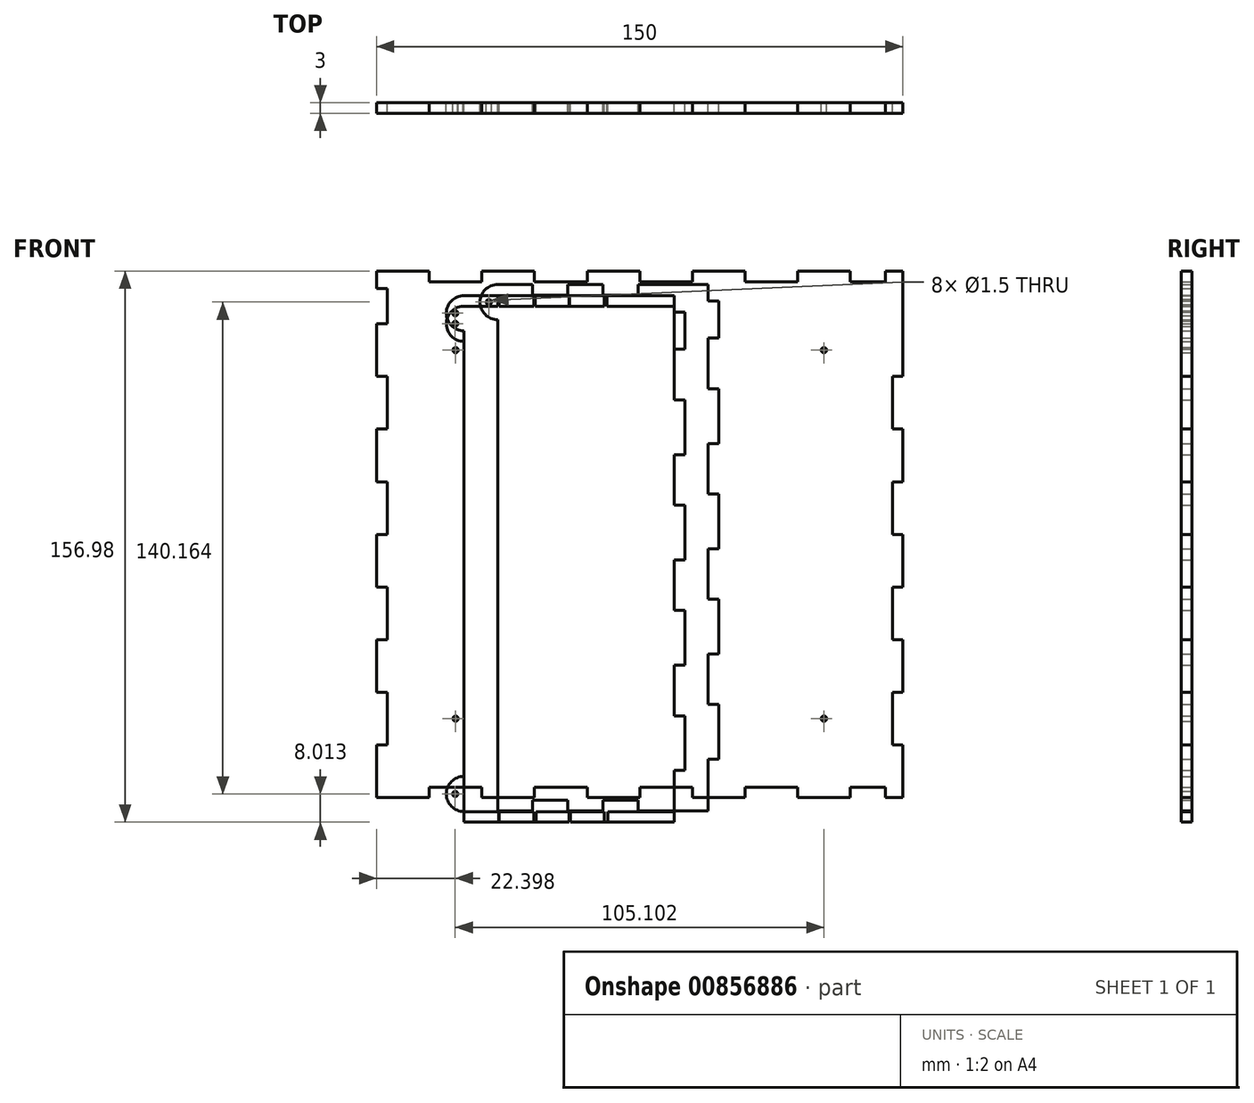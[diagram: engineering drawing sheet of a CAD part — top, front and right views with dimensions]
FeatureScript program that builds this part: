
annotation { "Feature Type Name" : "Feature", "Feature Type Description" : "" }
export const myFeature = defineFeature(function(context is Context, id is Id, definition is map)
    precondition{}
    {
        {
            var Q0;
            Q0=qCreatedBy(makeId("Front.planeOp"),FACE);
            var sketch = newSketch(context, id + "F0", { "sketchPlane" : qUnion([Q0])});
            skPoint(sketch, "E0.middle", {"position": v(0, 0) * mm});
            skLineSegment(sketch, "E1", {"start": v(-60, 72) * mm, "end": v(-45, 72) * mm});
            skLineSegment(sketch, "E2", {"start": v(-75, 75) * mm, "end": v(-60, 75) * mm});
            skLineSegment(sketch, "E3", {"start": v(-60, 75) * mm, "end": v(-60, 72) * mm});
            skLineSegment(sketch, "E4", {"start": v(-45, 72) * mm, "end": v(-45, 75) * mm});
            skLineSegment(sketch, "E5", {"start": v(-45, 75) * mm, "end": v(-30, 75) * mm});
            skLineSegment(sketch, "E6", {"start": v(-30, 75) * mm, "end": v(-30, 72) * mm});
            skLineSegment(sketch, "E7", {"start": v(-30, 72) * mm, "end": v(-15, 72) * mm});
            skLineSegment(sketch, "E8", {"start": v(-15, 72) * mm, "end": v(-15, 75) * mm});
            skLineSegment(sketch, "E9", {"start": v(-15, 75) * mm, "end": v(0, 75) * mm});
            skLineSegment(sketch, "E10", {"start": v(0, 75) * mm, "end": v(0, 72) * mm});
            skLineSegment(sketch, "E11", {"start": v(0, 72) * mm, "end": v(15, 72) * mm});
            skLineSegment(sketch, "E12", {"start": v(15, 72) * mm, "end": v(15, 75) * mm});
            skLineSegment(sketch, "E13", {"start": v(15, 75) * mm, "end": v(30, 75) * mm});
            skLineSegment(sketch, "E14", {"start": v(30, 75) * mm, "end": v(30, 72) * mm});
            skLineSegment(sketch, "E15", {"start": v(30, 72) * mm, "end": v(45, 72) * mm});
            skLineSegment(sketch, "E16", {"start": v(45, 72) * mm, "end": v(45, 75) * mm});
            skLineSegment(sketch, "E17", {"start": v(45, 75) * mm, "end": v(60, 75) * mm});
            skLineSegment(sketch, "E18", {"start": v(60, 75) * mm, "end": v(60, 72) * mm});
            skLineSegment(sketch, "E19", {"start": v(60, 72) * mm, "end": v(70, 72) * mm});
            skLineSegment(sketch, "E20", {"start": v(70, 72) * mm, "end": v(70, 75) * mm});
            skLineSegment(sketch, "E21", {"start": v(70, 75) * mm, "end": v(75, 75) * mm});
            skLineSegment(sketch, "E22", {"start": v(-72, -60) * mm, "end": v(-72, -45) * mm});
            skLineSegment(sketch, "E23", {"start": v(-75, -75) * mm, "end": v(-75, -60) * mm});
            skLineSegment(sketch, "E24", {"start": v(-75, -60) * mm, "end": v(-72, -60) * mm});
            skLineSegment(sketch, "E25", {"start": v(-72, -45) * mm, "end": v(-75, -45) * mm});
            skLineSegment(sketch, "E26", {"start": v(-75, -45) * mm, "end": v(-75, -30) * mm});
            skLineSegment(sketch, "E27", {"start": v(-75, -30) * mm, "end": v(-72, -30) * mm});
            skLineSegment(sketch, "E28", {"start": v(-72, -30) * mm, "end": v(-72, -15) * mm});
            skLineSegment(sketch, "E29", {"start": v(-72, -15) * mm, "end": v(-75, -15) * mm});
            skLineSegment(sketch, "E30", {"start": v(-75, -15) * mm, "end": v(-75, 0) * mm});
            skLineSegment(sketch, "E31", {"start": v(-75, 0) * mm, "end": v(-72, 0) * mm});
            skLineSegment(sketch, "E32", {"start": v(-72, 0) * mm, "end": v(-72, 15) * mm});
            skLineSegment(sketch, "E33", {"start": v(-72, 15) * mm, "end": v(-75, 15) * mm});
            skLineSegment(sketch, "E34", {"start": v(-75, 15) * mm, "end": v(-75, 30) * mm});
            skLineSegment(sketch, "E35", {"start": v(-75, 30) * mm, "end": v(-72, 30) * mm});
            skLineSegment(sketch, "E36", {"start": v(-72, 30) * mm, "end": v(-72, 45) * mm});
            skLineSegment(sketch, "E37", {"start": v(-72, 45) * mm, "end": v(-75, 45) * mm});
            skLineSegment(sketch, "E38", {"start": v(-75, 45) * mm, "end": v(-75, 60) * mm});
            skPoint(sketch, "E39.trimOffspring.end.orphan", {"position": v(-72, 75) * mm});
            skLineSegment(sketch, "E40", {"start": v(-75, 60) * mm, "end": v(-72, 60) * mm});
            skLineSegment(sketch, "E41", {"start": v(-72, 60) * mm, "end": v(-72, 70) * mm});
            skLineSegment(sketch, "E42", {"start": v(-72, 70) * mm, "end": v(-75, 70) * mm});
            skLineSegment(sketch, "E43", {"start": v(-75, 70) * mm, "end": v(-75, 75) * mm});
            skLineSegment(sketch, "E44", {"start": v(-75, 75) * mm, "end": v(-72, 75) * mm});
            skLineSegment(sketch, "E45.MirrorCS", {"start": v(75, 30) * mm, "end": v(72, 30) * mm});
            skLineSegment(sketch, "E46.MirrorCS", {"start": v(72, 45) * mm, "end": v(75, 45) * mm});
            skLineSegment(sketch, "E47.MirrorCS", {"start": v(75, 0) * mm, "end": v(72, 0) * mm});
            skLineSegment(sketch, "E48.MirrorCS", {"start": v(75, -60) * mm, "end": v(72, -60) * mm});
            skLineSegment(sketch, "E49.MirrorCS", {"start": v(72, 15) * mm, "end": v(75, 15) * mm});
            skLineSegment(sketch, "E50.MirrorCS", {"start": v(72, -45) * mm, "end": v(75, -45) * mm});
            skLineSegment(sketch, "E51.MirrorCS", {"start": v(75, -75) * mm, "end": v(75, -72) * mm});
            skLineSegment(sketch, "E52.MirrorCS", {"start": v(75, -30) * mm, "end": v(72, -30) * mm});
            skLineSegment(sketch, "E53.MirrorCS", {"start": v(75, 70) * mm, "end": v(75, 75) * mm});
            skLineSegment(sketch, "E54.MirrorCS", {"start": v(75, -75) * mm, "end": v(75, -60) * mm});
            skLineSegment(sketch, "E55.MirrorCS", {"start": v(72, -15) * mm, "end": v(75, -15) * mm});
            skLineSegment(sketch, "E56.MirrorCS", {"start": v(72, 0) * mm, "end": v(72, 15) * mm});
            skLineSegment(sketch, "E57.MirrorCS", {"start": v(72, 30) * mm, "end": v(72, 45) * mm});
            skLineSegment(sketch, "E58.MirrorCS", {"start": v(72, -60) * mm, "end": v(72, -45) * mm});
            skLineSegment(sketch, "E59.MirrorCS", {"start": v(72, -30) * mm, "end": v(72, -15) * mm});
            skLineSegment(sketch, "E60.MirrorCS", {"start": v(75, 15) * mm, "end": v(75, 30) * mm});
            skLineSegment(sketch, "E61.MirrorCS", {"start": v(75, -15) * mm, "end": v(75, 0) * mm});
            skPoint(sketch, "E62.MirrorP", {"position": v(75, -72) * mm});
            skLineSegment(sketch, "E63.MirrorCS", {"start": v(75, 45) * mm, "end": v(75, 60) * mm});
            skLineSegment(sketch, "E64.MirrorCS", {"start": v(75, -45) * mm, "end": v(75, -30) * mm});
            skLineSegment(sketch, "E65", {"start": v(75, 70) * mm, "end": v(75, 60) * mm});
            skPoint(sketch, "E66.start.orphan", {"position": v(-102.84, -173.45) * mm});
            skLineSegment(sketch, "E67.MirrorCS", {"start": v(45, -72) * mm, "end": v(45, -75) * mm});
            skLineSegment(sketch, "E68.MirrorCS", {"start": v(60, -75) * mm, "end": v(60, -72) * mm});
            skLineSegment(sketch, "E69.MirrorCS", {"start": v(15, -72) * mm, "end": v(15, -75) * mm});
            skLineSegment(sketch, "E70.MirrorCS", {"start": v(-60, -75) * mm, "end": v(-60, -72) * mm});
            skLineSegment(sketch, "E71.MirrorCS", {"start": v(-30, -75) * mm, "end": v(-30, -72) * mm});
            skLineSegment(sketch, "E72.MirrorCS", {"start": v(-15, -72) * mm, "end": v(-15, -75) * mm});
            skLineSegment(sketch, "E73.MirrorCS", {"start": v(0, -75) * mm, "end": v(0, -72) * mm});
            skLineSegment(sketch, "E74.MirrorCS", {"start": v(30, -75) * mm, "end": v(30, -72) * mm});
            skLineSegment(sketch, "E75.MirrorCS", {"start": v(-45, -72) * mm, "end": v(-45, -75) * mm});
            skLineSegment(sketch, "E76.MirrorCS", {"start": v(70, -72) * mm, "end": v(70, -75) * mm});
            skLineSegment(sketch, "E77.MirrorCS", {"start": v(-75, -75) * mm, "end": v(-72, -75) * mm});
            skLineSegment(sketch, "E78.MirrorCS", {"start": v(0, -72) * mm, "end": v(15, -72) * mm});
            skLineSegment(sketch, "E79.MirrorCS", {"start": v(70, -75) * mm, "end": v(75, -75) * mm});
            skLineSegment(sketch, "E80.MirrorCS", {"start": v(30, -72) * mm, "end": v(45, -72) * mm});
            skLineSegment(sketch, "E81.MirrorCS", {"start": v(-60, -72) * mm, "end": v(-45, -72) * mm});
            skLineSegment(sketch, "E82.MirrorCS", {"start": v(15, -75) * mm, "end": v(30, -75) * mm});
            skLineSegment(sketch, "E83.MirrorCS", {"start": v(-15, -75) * mm, "end": v(0, -75) * mm});
            skLineSegment(sketch, "E84.MirrorCS", {"start": v(45, -75) * mm, "end": v(60, -75) * mm});
            skLineSegment(sketch, "E85.MirrorCS", {"start": v(-75, -75) * mm, "end": v(-60, -75) * mm});
            skLineSegment(sketch, "E86.MirrorCS", {"start": v(-45, -75) * mm, "end": v(-30, -75) * mm});
            skLineSegment(sketch, "E87.MirrorCS", {"start": v(-30, -72) * mm, "end": v(-15, -72) * mm});
            skLineSegment(sketch, "E88.MirrorCS", {"start": v(60, -72) * mm, "end": v(70, -72) * mm});
            skPoint(sketch, "E89.MirrorP", {"position": v(-72, -75) * mm});
            skCircle(sketch, "E90", {"center": v(-52.5, -52.5) * mm, "radius": 0.75 * mm});
            skCircle(sketch, "E91", {"center": v(-52.5, 52.5) * mm, "radius": 0.75 * mm});
            skCircle(sketch, "E92", {"center": v(52.5, 52.5) * mm, "radius": 0.75 * mm});
            skCircle(sketch, "E93", {"center": v(52.5, -52.5) * mm, "radius": 0.75 * mm});
            skSolve(sketch);
        }
        {
            var Q0;
            Q0=qCreatedBy(makeId("Front.planeOp"),FACE);
            var sketch = newSketch(context, id + "F1", { "sketchPlane" : qUnion([Q0])});
            skPoint(sketch, "E94.start.orphan", {"position": v(-103.07, -194.53) * mm});
            skLineSegment(sketch, "E95", {"start": v(22.48, -63.79) * mm, "end": v(22.48, -48.79) * mm});
            skLineSegment(sketch, "E96", {"start": v(19.48, -78.79) * mm, "end": v(19.48, -64.09) * mm});
            skLineSegment(sketch, "E97", {"start": v(19.48, -48.49) * mm, "end": v(19.48, -34.09) * mm});
            skLineSegment(sketch, "E98", {"start": v(22.48, -33.79) * mm, "end": v(22.48, -18.79) * mm});
            skLineSegment(sketch, "E99", {"start": v(19.48, -18.49) * mm, "end": v(19.48, -4.09) * mm});
            skLineSegment(sketch, "E100", {"start": v(22.48, -3.79) * mm, "end": v(22.48, 11.21) * mm});
            skLineSegment(sketch, "E101", {"start": v(19.48, 11.51) * mm, "end": v(19.48, 25.91) * mm});
            skLineSegment(sketch, "E102", {"start": v(22.48, 26.21) * mm, "end": v(22.48, 41.21) * mm});
            skLineSegment(sketch, "E103", {"start": v(19.48, 41.51) * mm, "end": v(19.48, 55.91) * mm});
            skLineSegment(sketch, "E104", {"start": v(19.48, 66.51) * mm, "end": v(19.48, 71.21) * mm});
            skLineSegment(sketch, "E105", {"start": v(19.48, 71.21) * mm, "end": v(-0.52, 71.21) * mm});
            skLineSegment(sketch, "E106", {"start": v(-40.52, 61.19) * mm, "end": v(-40.52, -78.79) * mm});
            skLineSegment(sketch, "E107", {"start": v(19.48, -48.49) * mm, "end": v(22.48, -48.49) * mm});
            skLineSegment(sketch, "E108", {"start": v(22.48, -48.49) * mm, "end": v(22.48, -48.79) * mm});
            skPoint(sketch, "E109.start.orphan", {"position": v(19.48, -48.79) * mm});
            skLineSegment(sketch, "E110", {"start": v(19.48, -64.09) * mm, "end": v(22.48, -64.09) * mm});
            skLineSegment(sketch, "E111", {"start": v(22.48, -64.09) * mm, "end": v(22.48, -63.79) * mm});
            skLineSegment(sketch, "E112", {"start": v(19.48, -34.09) * mm, "end": v(22.48, -34.09) * mm});
            skLineSegment(sketch, "E113", {"start": v(22.48, -34.09) * mm, "end": v(22.48, -33.79) * mm});
            skLineSegment(sketch, "E114", {"start": v(19.48, -18.49) * mm, "end": v(22.48, -18.49) * mm});
            skLineSegment(sketch, "E115", {"start": v(22.48, -18.49) * mm, "end": v(22.48, -18.79) * mm});
            skPoint(sketch, "E116.orphan", {"position": v(19.48, -18.79) * mm});
            skLineSegment(sketch, "E117", {"start": v(22.48, -3.79) * mm, "end": v(22.48, -4.09) * mm});
            skLineSegment(sketch, "E118", {"start": v(22.48, -4.09) * mm, "end": v(19.48, -4.09) * mm});
            skLineSegment(sketch, "E119", {"start": v(22.48, 11.21) * mm, "end": v(22.48, 11.51) * mm});
            skLineSegment(sketch, "E120", {"start": v(22.48, 11.51) * mm, "end": v(19.48, 11.51) * mm});
            skLineSegment(sketch, "E121", {"start": v(22.48, 41.21) * mm, "end": v(22.48, 41.51) * mm});
            skLineSegment(sketch, "E122", {"start": v(22.48, 41.51) * mm, "end": v(19.48, 41.51) * mm});
            skLineSegment(sketch, "E123", {"start": v(22.48, 26.21) * mm, "end": v(22.48, 25.91) * mm});
            skLineSegment(sketch, "E124", {"start": v(22.48, 25.91) * mm, "end": v(19.48, 25.91) * mm});
            skPoint(sketch, "E125", {"position": v(-60.53, 71.19) * mm});
            skArc(sketch, "E126", {"start": v(-40.52, 71.21) * mm, "mid": v(-45.53, 66.2) * mm, "end": v(-40.52, 61.19) * mm});
            skCircle(sketch, "E127", {"center": v(-43, 66.2) * mm, "radius": 0.75 * mm});
            skPoint(sketch, "E128.orphan", {"position": v(-60.53, 66.19) * mm});
            skPoint(sketch, "E129.start.orphan", {"position": v(-60.53, 61.19) * mm});
            skLineSegment(sketch, "E130", {"start": v(-40.52, 71.21) * mm, "end": v(-30.52, 71.21) * mm});
            skLineSegment(sketch, "E131", {"start": v(-30.52, 71.21) * mm, "end": v(-30.52, 68.21) * mm});
            skLineSegment(sketch, "E132", {"start": v(-30.52, 68.21) * mm, "end": v(-20.52, 68.21) * mm});
            skLineSegment(sketch, "E133", {"start": v(-20.52, 68.21) * mm, "end": v(-20.52, 71.21) * mm});
            skLineSegment(sketch, "E134", {"start": v(-20.52, 71.21) * mm, "end": v(-10.52, 71.21) * mm});
            skLineSegment(sketch, "E135", {"start": v(-10.52, 71.21) * mm, "end": v(-10.52, 68.21) * mm});
            skLineSegment(sketch, "E136", {"start": v(-10.52, 68.21) * mm, "end": v(-0.52, 68.21) * mm});
            skLineSegment(sketch, "E137", {"start": v(-0.52, 68.21) * mm, "end": v(-0.52, 71.21) * mm});
            skLineSegment(sketch, "E138.trimOffspring", {"start": v(-30.52, 71.21) * mm, "end": v(-40.52, 71.21) * mm});
            skLineSegment(sketch, "E139.trimOffspring", {"start": v(-10.52, 71.21) * mm, "end": v(-20.52, 71.21) * mm});
            skLineSegment(sketch, "E140.MirrorCS", {"start": v(-10.52, -78.79) * mm, "end": v(-10.52, -75.79) * mm});
            skLineSegment(sketch, "E141.MirrorCS", {"start": v(-20.52, -75.79) * mm, "end": v(-20.52, -78.79) * mm});
            skLineSegment(sketch, "E142.MirrorCS", {"start": v(-0.52, -75.79) * mm, "end": v(-0.52, -78.79) * mm});
            skLineSegment(sketch, "E143.MirrorCS", {"start": v(-30.52, -78.79) * mm, "end": v(-30.52, -75.79) * mm});
            skLineSegment(sketch, "E144.MirrorCS", {"start": v(-10.52, -78.79) * mm, "end": v(-20.52, -78.79) * mm});
            skLineSegment(sketch, "E145.MirrorCS", {"start": v(-40.52, -78.79) * mm, "end": v(-30.52, -78.79) * mm});
            skLineSegment(sketch, "E146.MirrorCS", {"start": v(-10.52, -75.79) * mm, "end": v(-0.52, -75.79) * mm});
            skLineSegment(sketch, "E147.MirrorCS", {"start": v(-30.52, -78.79) * mm, "end": v(-40.52, -78.79) * mm});
            skLineSegment(sketch, "E148.MirrorCS", {"start": v(-30.52, -75.79) * mm, "end": v(-20.52, -75.79) * mm});
            skLineSegment(sketch, "E149.MirrorCS", {"start": v(19.48, -78.79) * mm, "end": v(-0.52, -78.79) * mm});
            skLineSegment(sketch, "E150.MirrorCS", {"start": v(-20.52, -78.79) * mm, "end": v(-10.52, -78.79) * mm});
            skLineSegment(sketch, "E151", {"start": v(22.48, 56.21) * mm, "end": v(22.48, 66.21) * mm});
            skLineSegment(sketch, "E152", {"start": v(22.48, 66.21) * mm, "end": v(22.48, 66.51) * mm});
            skLineSegment(sketch, "E153", {"start": v(22.48, 66.51) * mm, "end": v(19.48, 66.51) * mm});
            skLineSegment(sketch, "E154", {"start": v(22.48, 56.21) * mm, "end": v(22.48, 55.91) * mm});
            skLineSegment(sketch, "E155", {"start": v(22.48, 55.91) * mm, "end": v(19.48, 55.91) * mm});
            skSolve(sketch);
        }
        {
            var Q0;
            Q0=qCreatedBy(makeId("Front.planeOp"),FACE);
            var sketch = newSketch(context, id + "F2", { "sketchPlane" : qUnion([Q0])});
            skLineSegment(sketch, "E156", {"start": v(12.88, -66.98) * mm, "end": v(12.88, -51.98) * mm});
            skLineSegment(sketch, "E157", {"start": v(9.88, -81.98) * mm, "end": v(9.88, -67.28) * mm});
            skLineSegment(sketch, "E158", {"start": v(9.88, -51.68) * mm, "end": v(9.88, -37.28) * mm});
            skLineSegment(sketch, "E159", {"start": v(12.88, -36.98) * mm, "end": v(12.88, -21.98) * mm});
            skLineSegment(sketch, "E160", {"start": v(9.88, -21.68) * mm, "end": v(9.88, -7.28) * mm});
            skLineSegment(sketch, "E161", {"start": v(12.88, -6.98) * mm, "end": v(12.88, 8.02) * mm});
            skLineSegment(sketch, "E162", {"start": v(9.88, 8.32) * mm, "end": v(9.88, 22.72) * mm});
            skLineSegment(sketch, "E163", {"start": v(12.88, 23.02) * mm, "end": v(12.88, 38.02) * mm});
            skLineSegment(sketch, "E164", {"start": v(9.88, 38.32) * mm, "end": v(9.88, 52.72) * mm});
            skLineSegment(sketch, "E165", {"start": v(9.88, 63.32) * mm, "end": v(9.88, 68.02) * mm});
            skLineSegment(sketch, "E166", {"start": v(9.88, 68.02) * mm, "end": v(-10.12, 68.02) * mm});
            skLineSegment(sketch, "E167", {"start": v(-50.12, 58) * mm, "end": v(-50.12, -81.98) * mm});
            skLineSegment(sketch, "E168", {"start": v(9.88, -51.68) * mm, "end": v(12.88, -51.68) * mm});
            skLineSegment(sketch, "E169", {"start": v(12.88, -51.68) * mm, "end": v(12.88, -51.98) * mm});
            skPoint(sketch, "E170.start.orphan", {"position": v(9.88, -51.98) * mm});
            skLineSegment(sketch, "E171", {"start": v(9.88, -67.28) * mm, "end": v(12.88, -67.28) * mm});
            skLineSegment(sketch, "E172", {"start": v(12.88, -67.28) * mm, "end": v(12.88, -66.98) * mm});
            skLineSegment(sketch, "E173", {"start": v(9.88, -37.28) * mm, "end": v(12.88, -37.28) * mm});
            skLineSegment(sketch, "E174", {"start": v(12.88, -37.28) * mm, "end": v(12.88, -36.98) * mm});
            skLineSegment(sketch, "E175", {"start": v(9.88, -21.68) * mm, "end": v(12.88, -21.68) * mm});
            skLineSegment(sketch, "E176", {"start": v(12.88, -21.68) * mm, "end": v(12.88, -21.98) * mm});
            skPoint(sketch, "E177.orphan", {"position": v(9.88, -21.98) * mm});
            skLineSegment(sketch, "E178", {"start": v(12.88, -6.98) * mm, "end": v(12.88, -7.28) * mm});
            skLineSegment(sketch, "E179", {"start": v(12.88, -7.28) * mm, "end": v(9.88, -7.28) * mm});
            skLineSegment(sketch, "E180", {"start": v(12.88, 8.02) * mm, "end": v(12.88, 8.32) * mm});
            skLineSegment(sketch, "E181", {"start": v(12.88, 8.32) * mm, "end": v(9.88, 8.32) * mm});
            skLineSegment(sketch, "E182", {"start": v(12.88, 38.02) * mm, "end": v(12.88, 38.32) * mm});
            skLineSegment(sketch, "E183", {"start": v(12.88, 38.32) * mm, "end": v(9.88, 38.32) * mm});
            skLineSegment(sketch, "E184", {"start": v(12.88, 23.02) * mm, "end": v(12.88, 22.72) * mm});
            skLineSegment(sketch, "E185", {"start": v(12.88, 22.72) * mm, "end": v(9.88, 22.72) * mm});
            skPoint(sketch, "E186", {"position": v(-70.13, 68) * mm});
            skArc(sketch, "E187", {"start": v(-50.12, 68.02) * mm, "mid": v(-55.13, 63.01) * mm, "end": v(-50.12, 58) * mm});
            skCircle(sketch, "E188", {"center": v(-52.6, 63.01) * mm, "radius": 0.75 * mm});
            skPoint(sketch, "E189.orphan", {"position": v(-70.13, 63) * mm});
            skPoint(sketch, "E190.start.orphan", {"position": v(-70.13, 58) * mm});
            skLineSegment(sketch, "E191", {"start": v(9.88, 63.32) * mm, "end": v(9.88, 52.72) * mm});
            skLineSegment(sketch, "E192", {"start": v(-50.12, 68.02) * mm, "end": v(-40.12, 68.02) * mm});
            skLineSegment(sketch, "E193", {"start": v(-40.12, 68.02) * mm, "end": v(-40.12, 65.02) * mm});
            skLineSegment(sketch, "E194", {"start": v(-40.12, 65.02) * mm, "end": v(-30.12, 65.02) * mm});
            skLineSegment(sketch, "E195", {"start": v(-30.12, 65.02) * mm, "end": v(-30.12, 68.02) * mm});
            skLineSegment(sketch, "E196", {"start": v(-30.12, 68.02) * mm, "end": v(-20.12, 68.02) * mm});
            skLineSegment(sketch, "E197", {"start": v(-20.12, 68.02) * mm, "end": v(-20.12, 65.02) * mm});
            skLineSegment(sketch, "E198", {"start": v(-20.12, 65.02) * mm, "end": v(-10.12, 65.02) * mm});
            skLineSegment(sketch, "E199", {"start": v(-10.12, 65.02) * mm, "end": v(-10.12, 68.02) * mm});
            skLineSegment(sketch, "E200.trimOffspring", {"start": v(-40.12, 68.02) * mm, "end": v(-50.12, 68.02) * mm});
            skLineSegment(sketch, "E201.trimOffspring", {"start": v(-20.12, 68.02) * mm, "end": v(-30.12, 68.02) * mm});
            skLineSegment(sketch, "E202.MirrorCS", {"start": v(-20.12, -81.98) * mm, "end": v(-20.12, -78.98) * mm});
            skLineSegment(sketch, "E203.MirrorCS", {"start": v(-30.12, -78.98) * mm, "end": v(-30.12, -81.98) * mm});
            skLineSegment(sketch, "E204.MirrorCS", {"start": v(-10.12, -78.98) * mm, "end": v(-10.12, -81.98) * mm});
            skLineSegment(sketch, "E205.MirrorCS", {"start": v(-40.12, -81.98) * mm, "end": v(-40.12, -78.98) * mm});
            skLineSegment(sketch, "E206.MirrorCS", {"start": v(-20.12, -81.98) * mm, "end": v(-30.12, -81.98) * mm});
            skLineSegment(sketch, "E207.MirrorCS", {"start": v(-50.12, -81.98) * mm, "end": v(-40.12, -81.98) * mm});
            skLineSegment(sketch, "E208.MirrorCS", {"start": v(-20.12, -78.98) * mm, "end": v(-10.12, -78.98) * mm});
            skLineSegment(sketch, "E209.MirrorCS", {"start": v(-40.12, -81.98) * mm, "end": v(-50.12, -81.98) * mm});
            skLineSegment(sketch, "E210.MirrorCS", {"start": v(-40.12, -78.98) * mm, "end": v(-30.12, -78.98) * mm});
            skLineSegment(sketch, "E211.MirrorCS", {"start": v(9.88, -81.98) * mm, "end": v(-10.12, -81.98) * mm});
            skLineSegment(sketch, "E212.MirrorCS", {"start": v(-30.12, -81.98) * mm, "end": v(-20.12, -81.98) * mm});
            skSolve(sketch);
        }
        {
            var Q0;
            Q0=qCreatedBy(makeId("Front.planeOp"),FACE);
            var sketch = newSketch(context, id + "F3", { "sketchPlane" : qUnion([Q0])});
            skLineSegment(sketch, "E213", {"start": v(12.88, -66.98) * mm, "end": v(12.88, -51.98) * mm});
            skLineSegment(sketch, "E214", {"start": v(9.88, -78.98) * mm, "end": v(9.88, -67.28) * mm});
            skLineSegment(sketch, "E215", {"start": v(9.88, -51.68) * mm, "end": v(9.88, -37.28) * mm});
            skLineSegment(sketch, "E216", {"start": v(12.88, -36.98) * mm, "end": v(12.88, -21.98) * mm});
            skLineSegment(sketch, "E217", {"start": v(9.88, -21.68) * mm, "end": v(9.88, -7.28) * mm});
            skLineSegment(sketch, "E218", {"start": v(12.88, -6.98) * mm, "end": v(12.88, 8.02) * mm});
            skLineSegment(sketch, "E219", {"start": v(9.88, 8.32) * mm, "end": v(9.88, 22.72) * mm});
            skLineSegment(sketch, "E220", {"start": v(12.88, 23.02) * mm, "end": v(12.88, 38.02) * mm});
            skLineSegment(sketch, "E221", {"start": v(9.88, 38.32) * mm, "end": v(9.88, 52.72) * mm});
            skLineSegment(sketch, "E222", {"start": v(12.88, 53.02) * mm, "end": v(12.88, 63.02) * mm});
            skLineSegment(sketch, "E223", {"start": v(9.88, 63.32) * mm, "end": v(9.88, 65.02) * mm});
            skPoint(sketch, "E224.start.orphan", {"position": v(-17.96, -180.43) * mm});
            skLineSegment(sketch, "E225", {"start": v(-50.12, 55) * mm, "end": v(-50.12, -68.95) * mm});
            skLineSegment(sketch, "E226", {"start": v(9.88, -51.68) * mm, "end": v(12.88, -51.68) * mm});
            skLineSegment(sketch, "E227", {"start": v(12.88, -51.68) * mm, "end": v(12.88, -51.98) * mm});
            skPoint(sketch, "E228.start.orphan", {"position": v(9.88, -51.98) * mm});
            skLineSegment(sketch, "E229", {"start": v(9.88, -67.28) * mm, "end": v(12.88, -67.28) * mm});
            skLineSegment(sketch, "E230", {"start": v(12.88, -67.28) * mm, "end": v(12.88, -66.98) * mm});
            skLineSegment(sketch, "E231", {"start": v(9.88, -37.28) * mm, "end": v(12.88, -37.28) * mm});
            skLineSegment(sketch, "E232", {"start": v(12.88, -37.28) * mm, "end": v(12.88, -36.98) * mm});
            skLineSegment(sketch, "E233", {"start": v(9.88, -21.68) * mm, "end": v(12.88, -21.68) * mm});
            skLineSegment(sketch, "E234", {"start": v(12.88, -21.68) * mm, "end": v(12.88, -21.98) * mm});
            skPoint(sketch, "E235.orphan", {"position": v(9.88, -21.98) * mm});
            skLineSegment(sketch, "E236", {"start": v(12.88, -6.98) * mm, "end": v(12.88, -7.28) * mm});
            skLineSegment(sketch, "E237", {"start": v(12.88, -7.28) * mm, "end": v(9.88, -7.28) * mm});
            skLineSegment(sketch, "E238", {"start": v(12.88, 8.02) * mm, "end": v(12.88, 8.32) * mm});
            skLineSegment(sketch, "E239", {"start": v(12.88, 8.32) * mm, "end": v(9.88, 8.32) * mm});
            skLineSegment(sketch, "E240", {"start": v(12.88, 38.02) * mm, "end": v(12.88, 38.32) * mm});
            skLineSegment(sketch, "E241", {"start": v(12.88, 38.32) * mm, "end": v(9.88, 38.32) * mm});
            skLineSegment(sketch, "E242", {"start": v(12.88, 23.02) * mm, "end": v(12.88, 22.72) * mm});
            skLineSegment(sketch, "E243", {"start": v(12.88, 22.72) * mm, "end": v(9.88, 22.72) * mm});
            skLineSegment(sketch, "E244", {"start": v(12.88, 63.02) * mm, "end": v(12.88, 63.32) * mm});
            skLineSegment(sketch, "E245", {"start": v(12.88, 63.32) * mm, "end": v(9.88, 63.32) * mm});
            skLineSegment(sketch, "E246", {"start": v(12.88, 53.02) * mm, "end": v(12.88, 52.72) * mm});
            skLineSegment(sketch, "E247", {"start": v(12.88, 52.72) * mm, "end": v(9.88, 52.72) * mm});
            skArc(sketch, "E248", {"start": v(-50.39, 65.02) * mm, "mid": v(-55.13, 59.88) * mm, "end": v(-50.12, 55) * mm});
            skCircle(sketch, "E249", {"center": v(-52.6, 60.01) * mm, "radius": 0.75 * mm});
            skArc(sketch, "E250", {"start": v(-50.12, -68.95) * mm, "mid": v(-55.13, -73.97) * mm, "end": v(-50.12, -78.98) * mm});
            skCircle(sketch, "E251", {"center": v(-52.6, -73.97) * mm, "radius": 0.75 * mm});
            skLineSegment(sketch, "E252", {"start": v(-50.12, 65.02) * mm, "end": v(-40.44, 65.02) * mm});
            skLineSegment(sketch, "E253", {"start": v(-50.39, 65.02) * mm, "end": v(-40.44, 65.02) * mm});
            skLineSegment(sketch, "E254.trimOffspring", {"start": v(-9.38, 65.02) * mm, "end": v(9.88, 65.02) * mm});
            skLineSegment(sketch, "E255", {"start": v(-20.12, 65.02) * mm, "end": v(-20.12, 65.02) * mm});
            skLineSegment(sketch, "E256", {"start": v(-40.44, 65.02) * mm, "end": v(-40.44, 68.02) * mm});
            skLineSegment(sketch, "E257", {"start": v(-40.44, 68.02) * mm, "end": v(-30.44, 68.02) * mm});
            skLineSegment(sketch, "E258", {"start": v(-30.44, 68.02) * mm, "end": v(-30.12, 68.02) * mm});
            skLineSegment(sketch, "E259", {"start": v(-30.12, 68.02) * mm, "end": v(-29.8, 68.02) * mm});
            skLineSegment(sketch, "E260", {"start": v(-29.8, 68.02) * mm, "end": v(-29.8, 65.02) * mm});
            skLineSegment(sketch, "E261", {"start": v(-20.02, 65.02) * mm, "end": v(-20.02, 68.02) * mm});
            skLineSegment(sketch, "E262", {"start": v(-9.38, 68.02) * mm, "end": v(-9.38, 65.02) * mm});
            skPoint(sketch, "E263.start.orphan", {"position": v(-40.12, 65.02) * mm});
            skPoint(sketch, "E264.orphan", {"position": v(-35.12, 65.02) * mm});
            skPoint(sketch, "E265.orphan", {"position": v(-30.12, 65.02) * mm});
            skPoint(sketch, "E266.end.orphan", {"position": v(-15.12, 65.02) * mm});
            skPoint(sketch, "E267.start.orphan", {"position": v(-25.12, 65.02) * mm});
            skPoint(sketch, "E268.end.orphan", {"position": v(-10.12, 65.02) * mm});
            skLineSegment(sketch, "E269", {"start": v(-20.02, 68.02) * mm, "end": v(-9.38, 68.02) * mm});
            skLineSegment(sketch, "E270", {"start": v(-29.8, 65.02) * mm, "end": v(-20.02, 65.02) * mm});
            skLineSegment(sketch, "E271.MirrorCS", {"start": v(-19.75, -78.98) * mm, "end": v(-19.75, -81.98) * mm});
            skLineSegment(sketch, "E272.MirrorCS", {"start": v(-30.17, -81.98) * mm, "end": v(-29.85, -81.98) * mm});
            skLineSegment(sketch, "E273.MirrorCS", {"start": v(-19.86, -78.98) * mm, "end": v(-19.86, -78.98) * mm});
            skLineSegment(sketch, "E274.MirrorCS", {"start": v(-29.53, -81.98) * mm, "end": v(-29.53, -78.98) * mm});
            skLineSegment(sketch, "E275.MirrorCS", {"start": v(-29.85, -81.98) * mm, "end": v(-29.53, -81.98) * mm});
            skLineSegment(sketch, "E276.MirrorCS", {"start": v(-40.17, -78.98) * mm, "end": v(-40.17, -81.98) * mm});
            skLineSegment(sketch, "E277.MirrorCS", {"start": v(-9.11, -81.98) * mm, "end": v(-9.11, -78.98) * mm});
            skLineSegment(sketch, "E278.MirrorCS", {"start": v(-19.75, -81.98) * mm, "end": v(-9.11, -81.98) * mm});
            skLineSegment(sketch, "E279.MirrorCS", {"start": v(-29.53, -78.98) * mm, "end": v(-19.75, -78.98) * mm});
            skLineSegment(sketch, "E280.MirrorCS", {"start": v(-40.17, -81.98) * mm, "end": v(-30.17, -81.98) * mm});
            skLineSegment(sketch, "E281.MirrorCS", {"start": v(-50.12, -78.98) * mm, "end": v(-40.17, -78.98) * mm});
            skLineSegment(sketch, "E282.MirrorCS", {"start": v(-9.11, -78.98) * mm, "end": v(10.15, -78.98) * mm});
            skLineSegment(sketch, "E283.MirrorCS", {"start": v(-49.85, -78.98) * mm, "end": v(-40.17, -78.98) * mm});
            skSolve(sketch);
        }
        {
            var Q0;
            Q0 = qSketchRegion(id + "F0", true);
            extrude(context, id + "F4", {"entities" : qUnion([Q0]), "depth" : 3 * mm, "offsetDistance" : 25 * mm});
        }
        {
            var Q0;
            Q0 = qSketchRegion(id + "F1", true);
            extrude(context, id + "F5", {"entities" : qUnion([Q0]), "depth" : 3 * mm, "offsetDistance" : 25 * mm});
        }
        {
            var Q0;
            Q0 = qSketchRegion(id + "F2", true);
            extrude(context, id + "F6", {"entities" : qUnion([Q0]), "depth" : 3 * mm, "offsetDistance" : 25 * mm});
        }
        {
            var Q0;
            Q0 = qSketchRegion(id + "F3", true);
            extrude(context, id + "F7", {"entities" : qUnion([Q0]), "depth" : 3 * mm, "offsetDistance" : 25 * mm});
        }
    });
